# Revit family: Water_Heaters_HAJDU_HAJDU-STA-C-SZTEA_
name_source: partatom
category: Mechanical Equipment
units: mm (PartAtom-declared; Revit-internal decimal feet)

## family parameters
Always vertical = Yes
Classification = None
Cut with Voids When Loaded = No
Maintain Annotation Orientation = No
OmniClass Number = 23.31.29.13
OmniClass Title = Hot Water Tank Heaters
Part Type = Normal
Room Calculation Point = No
Round Connector Dimension = Use Diameter
Shared = No
Work Plane-Based = Yes

## types (2) — shared parameters
Case Material = Hajdu - Felület - Fehér
Církulációs csonk = 19.05 mm  [stored 0.0625 ft]
Default Elevation = 1219.2 mm  [stored 4 ft]
Description = A HAJDU multienergiás, nagy űrtartalmú szolár STA...C tartályok alsó harmadában található egy csőkígyó, ami indirekt módon felfűti a tartályban található használati melegvizet. Szolár rendszerbe köthető; Aktív anódos korrózió védelem.
Elektromos futopatron csatlakozás = 38.1 mm  [stored 0.125 ft]
Energiahatékonysági osztály = C
Hocserélo csatlakozás = 19.05 mm  [stored 0.0625 ft]
Homéro csonk = 12.7 mm  [stored 0.0416667 ft]
Manufacturer = HAJDU
Product Page URL = https://hajdurt.hu
URL = https://hajdurt.hu
Vízcsatlakozás = 19.05 mm  [stored 0.0625 ft]
Érzékelo tokcso = 12.7 mm  [stored 0.0416667 ft]
Üzemi nyomás = 0.6 MPa

## per-type parameters (varying)
| type | Csatlakozó magassága "A" | Csatlakozó magassága "B" | Csatlakozó magassága "C" | Csatlakozó magassága "E" | Csatlakozó magassága "F" | Csatlakozó magassága "G" | Csatlakozó magassága "I" | Csúcsteljesítmény | Hocserélo felulete | Hocserélo névleges urtartalma | Hocserélo tartós teljesítmény | Hocserélo áramlási ellenállása max. | Magasság | Névleges urtartalom | Rádiusz | Tartos teljesítmény | Tárolási veszteség | Tömeg | Átméro |
| STA 200C SZTEA | 220 mm  [stored 0.721785 ft] | 570 mm  [stored 1.87008 ft] | 880 mm  [stored 2.88714 ft] | 416 mm | 975 mm  [stored 3.19882 ft] | 1403 mm  [stored 4.60302 ft] | 840 mm  [stored 2.75591 ft] | 340 liter/az elso 10 perc | 1 m2 | 7 l | 60 kW | 90 mbar | 1530 mm  [stored 5.01969 ft] | 200 l | 275 mm | 735 liter/h | 71 W | 73.00 kg | 550 mm |
| STA 300C SZTEA | 210 mm  [stored 0.688976 ft] | 630 mm  [stored 2.06693 ft] | 930 mm  [stored 3.05118 ft] | 364 mm  [stored 1.19423 ft] | 1025 mm  [stored 3.36286 ft] | 1387 mm  [stored 4.55052 ft] | 890 mm  [stored 2.91995 ft] | 510 liter/az elso 10 perc | 1.5 m2 | 10.5 l | 45 kW | 130 mbar | 1535 mm  [stored 5.03609 ft] | 300 l | 332.5 mm  [stored 1.09088 ft] | 1100 liter/h | 94 W | 93.00 kg | 665 mm  [stored 2.18176 ft] |

note: column(s) folded — value = type name in every type: Model

note: [stored X ft] marks values corroborated as IEEE doubles in the binary element streams (Revit-internal decimal feet)

## geometry (parser evidence)
native form markers: Sweep x3
no freeform markers — native parametric forms only
